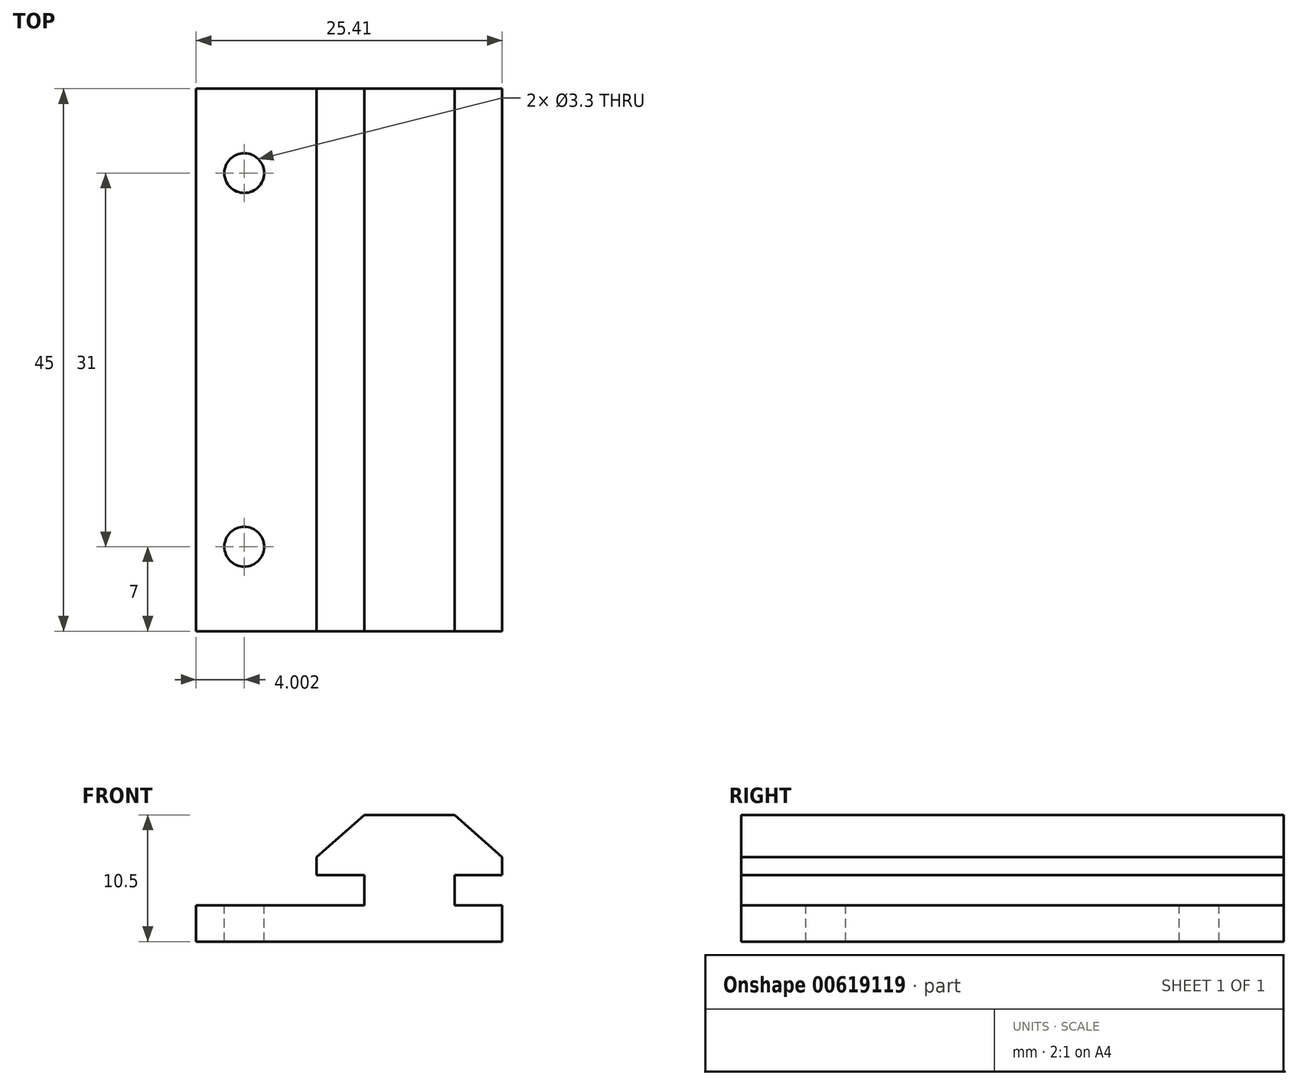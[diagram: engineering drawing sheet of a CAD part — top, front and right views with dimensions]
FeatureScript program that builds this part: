
annotation { "Feature Type Name" : "Feature", "Feature Type Description" : "" }
export const myFeature = defineFeature(function(context is Context, id is Id, definition is map)
    precondition{}
    {
        {
            var Q0;
            Q0=qCreatedBy(makeId("Front.planeOp"),FACE);
            var sketch = newSketch(context, id + "F0", { "sketchPlane" : qUnion([Q0])});
            skLineSegment(sketch, "E0", {"start": v(-4.96, 0) * mm, "end": v(-4.96, 2.5) * mm});
            skLineSegment(sketch, "E1", {"start": v(-4.96, 2.5) * mm, "end": v(-8.92, 2.5) * mm});
            skLineSegment(sketch, "E2", {"start": v(-8.92, 2.5) * mm, "end": v(-8.92, 4) * mm});
            skLineSegment(sketch, "E3", {"start": v(-8.92, 4) * mm, "end": v(-4.96, 7.5) * mm});
            skLineSegment(sketch, "E4", {"start": v(-4.96, 7.5) * mm, "end": v(2.54, 7.5) * mm});
            skLineSegment(sketch, "E5", {"start": v(2.54, 7.5) * mm, "end": v(6.49, 4) * mm});
            skLineSegment(sketch, "E6", {"start": v(6.49, 4) * mm, "end": v(6.49, 2.5) * mm});
            skLineSegment(sketch, "E7", {"start": v(6.49, 2.5) * mm, "end": v(2.54, 2.5) * mm});
            skLineSegment(sketch, "E8", {"start": v(2.54, 2.5) * mm, "end": v(2.54, 0) * mm});
            skLineSegment(sketch, "E9", {"start": v(2.54, 0) * mm, "end": v(-4.96, 0) * mm});
            skLineSegment(sketch, "E10.bottom", {"start": v(-8.92, 0) * mm, "end": v(6.49, 0) * mm});
            skLineSegment(sketch, "E10.top", {"start": v(-8.92, -3) * mm, "end": v(6.49, -3) * mm});
            skLineSegment(sketch, "E10.left", {"start": v(-8.92, 0) * mm, "end": v(-8.92, -3) * mm});
            skLineSegment(sketch, "E10.right", {"start": v(6.49, 0) * mm, "end": v(6.49, -3) * mm});
            skSolve(sketch);
        }
        {
            var Q0;
            Q0=qSketchRegion(id+"F0",true);
            extrude(context, id + "F1", {"entities" : qUnion([Q0]), "depth" : 45 * mm, "offsetDistance" : 25 * mm});
        }
        {
            var Q0;
            Q0=makeQuery(id+"F1.opExtrude","SWEPT_FACE",FACE,{"disambiguationData":[OSD([sQuery(id+"F0.wireOp",EDGE,"E10.left")])]});
            var sketch = newSketch(context, id + "F2", { "sketchPlane" : qUnion([Q0])});
            skLineSegment(sketch, "E11.bottom", {"start": v(0, 0) * mm, "end": v(45, 0) * mm});
            skLineSegment(sketch, "E11.top", {"start": v(0, -3) * mm, "end": v(45, -3) * mm});
            skLineSegment(sketch, "E11.left", {"start": v(0, 0) * mm, "end": v(0, -3) * mm});
            skLineSegment(sketch, "E11.right", {"start": v(45, 0) * mm, "end": v(45, -3) * mm});
            skSolve(sketch);
        }
        {
            var Q0;
            Q0 = qSketchRegion(id + "F2", true);
            extrude(context, id + "F3", {"entities" : qUnion([Q0]), "operationType" : NewBodyOperationType.ADD, "depth" : 10 * mm, "offsetDistance" : 25 * mm});
        }
        {
            var Q0;
            Q0=makeQuery(id+"F3.boolean.opBoolean","MERGE",FACE,{"derivedFrom":[makeQuery(id+"F1.opExtrude","SWEPT_FACE",FACE,{"disambiguationData":[OSD([sQuery(id+"F0.wireOp",EDGE,"E10.top")])]}),makeQuery(id+"F3.opExtrude","SWEPT_FACE",FACE,{"disambiguationData":[OSD([sQuery(id+"F2.wireOp",EDGE,"E11.top")])]})]});
            var sketch = newSketch(context, id + "F4", { "sketchPlane" : qUnion([Q0])});
            skPoint(sketch, "E12", {"position": v(-18.92, 22.5) * mm});
            skPoint(sketch, "E13", {"position": v(-14.92, 38) * mm});
            skPoint(sketch, "E14", {"position": v(-14.92, 7) * mm});
            skSolve(sketch);
        }
        {
            var Q0;
            Q0=sQuery(id+"F4.wireOp",VERTEX,"E13");
            var Q1;
            Q1=sQuery(id+"F4.wireOp",VERTEX,"E14");
            var Q2;
            Q2=makeQuery(id+"F1.opExtrude","SWEPT_BODY",BODY,{"disambiguationData":[OSD([sQuery(id+"F0.wireOp",EDGE,"E0"),sQuery(id+"F0.wireOp",EDGE,"E1"),sQuery(id+"F0.wireOp",EDGE,"E2"),sQuery(id+"F0.wireOp",EDGE,"E3"),sQuery(id+"F0.wireOp",EDGE,"E4"),sQuery(id+"F0.wireOp",EDGE,"E5"),sQuery(id+"F0.wireOp",EDGE,"E6"),sQuery(id+"F0.wireOp",EDGE,"E7"),sQuery(id+"F0.wireOp",EDGE,"E8"),sQuery(id+"F0.wireOp",EDGE,"E10.bottom"),sQuery(id+"F0.wireOp",EDGE,"E10.top"),sQuery(id+"F0.wireOp",EDGE,"E10.left"),sQuery(id+"F0.wireOp",EDGE,"E10.right")])]});
            hole(context, id + "F5", {"style" : HoleStyle.SIMPLE, "endStyle" : HoleEndStyle.THROUGH, "standardTappedOrClearance" : lookupTablePath({ "standard" : "ISO", "fit" : "Normal", "size" : "M3", "type" : "Clearance" }), "standardBlindInLast" : lookupTablePath({ "fit" : "Standard", "standard" : "ISO", "size" : "M3", "type" : "Clearance" }), "holeDiameter" : 3.3 * mm, "majorDiameter" : 5 * mm, "isTappedThrough" : true, "tappedDepth" : 12 * mm, "tapClearance" : 3, "locations" : qUnion([Q0, Q1]), "scope" : qUnion([Q2]), "startStyle" : HoleStartStyle.SKETCH});
        }
    });
